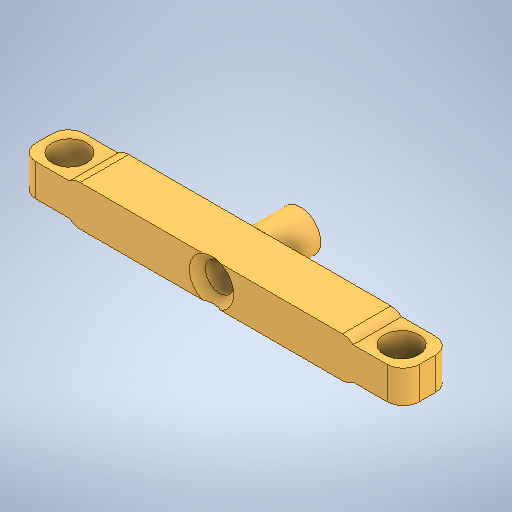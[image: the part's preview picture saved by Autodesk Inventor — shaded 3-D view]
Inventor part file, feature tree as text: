
AUTODESK INVENTOR PART (.ipt)
format: ipt  version: 2025.2 (Build 292293000, 293)  size: 370,688 bytes
history: native  units: in
note: dims shown in document units (in); Inventor stores cm internally (conversion verified against a paired STEP export)
features: fillet x6, move_body x6, extrude x5, sketch x5, direct_edit x1, other x1
ambient origin geometry x8: Origin, YZ Plane, XZ Plane, XY Plane, X Axis, Y Axis, Z Axis, Center Point
bodies: Solid1 (feature_tree)
feature tree (24):
  extrude  "Extrusion1"  Depth=0.1693in
  extrude  "Extrusion2"  Depth=0.2362in
  extrude  "Extrusion3"  Depth=0.2362in
  fillet  "Fillet1"  Radius=0.2362in
  fillet  "Fillet2"  Radius=0.0197in
  direct_edit  "Direct Edit1"
  fillet  "Fillet3"  Radius=0.2362in
  fillet  "Fillet4"  Radius=0.2362in
  fillet  "Fillet5"  Radius=0.2362in
  fillet  "Fillet6"  Radius=0.2362in
  extrude  "Extrusion4"  Depth=0.0787in
  extrude  "Extrusion5"  Depth=0.0197in TaperAngle=0.0deg
  sketch  "Sketch1"  dims[d0=0.1693in d1=0.1693in]
  sketch  "Sketch2"  dims[d2=0.1969in d3=0.0in d4=0.2362in]
  sketch  "Sketch3"  dims[d5=0.2362in d6=0.2362in d7=0.2362in d8=0.0197in d9=0.0in d10=0.2362in d11=0.2362in d12=0.2362in d13=0.2362in]
  sketch  "Sketch4"  dims[d14=0.0197in d15=0.0in d16=0.0787in]
  sketch  "Sketch5"  dims[d17=0.0787in d18=0.0in d19=0.0in d20=0.0197in d21=0.0in d22=0.0in d23=0.0197in d24=0.0787in d25=0.0787in d26=0.0787in d27=0.0787in d28=0.0in d29=0.0in d30=0.0197in d31=0.0in d32=0.0in d33=0.0197in d34=0.0in d35=0.0in d36=-0.0118in d37=0.0in d38=0.0in d39=-0.0118in d41=0.0315in d42=0.0in d43=0.1378in d44=0.0394in d45=0.0in]
  other  "Com_MagnetMount"
  move_body  "Move1"
  move_body  "Move2"
  move_body  "Move3"
  move_body  "Move4"
  move_body  "Move5"
  move_body  "Move6"
